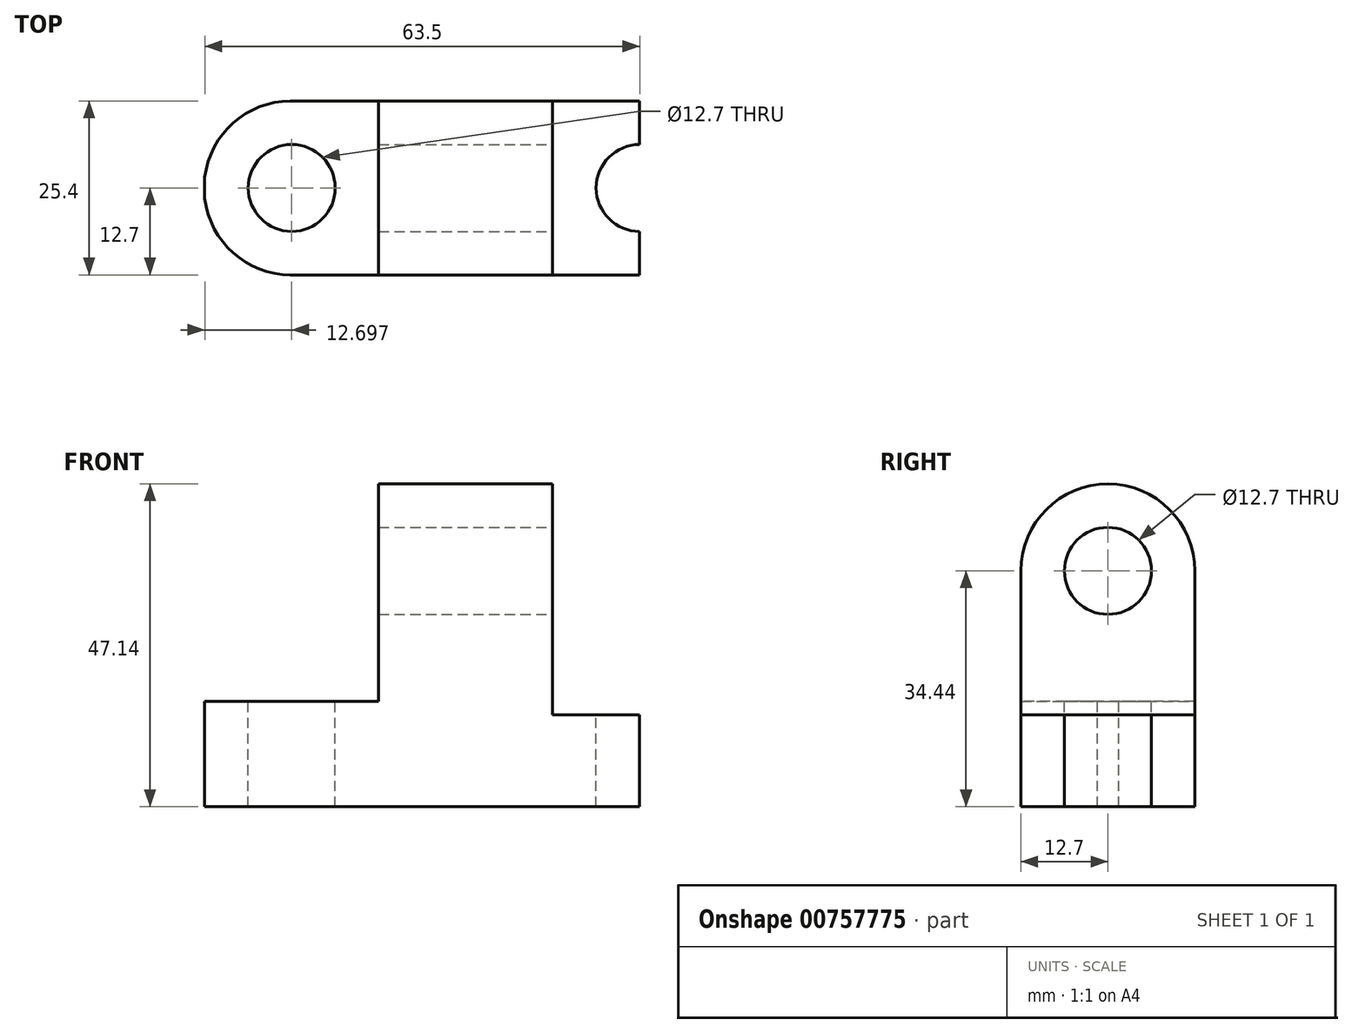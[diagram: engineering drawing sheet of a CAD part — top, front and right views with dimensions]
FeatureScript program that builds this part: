
annotation { "Feature Type Name" : "Feature", "Feature Type Description" : "" }
export const myFeature = defineFeature(function(context is Context, id is Id, definition is map)
    precondition{}
    {
        {
            var Q0;
            Q0=qCreatedBy(makeId("Front.planeOp"),FACE);
            var sketch = newSketch(context, id + "F0", { "sketchPlane" : qUnion([Q0])});
            skLineSegment(sketch, "E0", {"start": v(-30.36, 0) * mm, "end": v(45.84, 0) * mm});
            skLineSegment(sketch, "E1", {"start": v(45.84, 0) * mm, "end": v(45.84, 13.4) * mm});
            skLineSegment(sketch, "E2", {"start": v(45.84, 13.4) * mm, "end": v(20.44, 13.4) * mm});
            skLineSegment(sketch, "E3", {"start": v(20.44, 13.4) * mm, "end": v(20.44, 47.14) * mm});
            skLineSegment(sketch, "E4", {"start": v(20.44, 47.14) * mm, "end": v(-4.96, 47.14) * mm});
            skLineSegment(sketch, "E5", {"start": v(-4.96, 47.14) * mm, "end": v(-4.96, 15.39) * mm});
            skLineSegment(sketch, "E6", {"start": v(-4.96, 15.39) * mm, "end": v(-30.36, 15.39) * mm});
            skLineSegment(sketch, "E7", {"start": v(-30.36, 15.39) * mm, "end": v(-30.36, 0) * mm});
            skSolve(sketch);
        }
        {
            var Q0;
            Q0 = qSketchRegion(id + "F0", true);
            extrude(context, id + "F1", {"entities" : qUnion([Q0]), "depth" : 25.4 * mm, "offsetDistance" : 25.4 * mm});
        }
        {
            var Q0;
            Q0=makeQuery(id+"F1.opExtrude","SWEPT_FACE",FACE,{"disambiguationData":[OSD([sQuery(id+"F0.wireOp",EDGE,"E3")])]});
            var sketch = newSketch(context, id + "F2", { "sketchPlane" : qUnion([Q0])});
            skLineSegment(sketch, "E8", {"start": v(-25.4, 34.44) * mm, "end": v(0, 34.44) * mm});
            skCircle(sketch, "E9", {"center": v(-12.7, 34.44) * mm, "radius": 6.35 * mm});
            skArc(sketch, "E10", {"start": v(0, 34.44) * mm, "mid": v(-12.7, 47.14) * mm, "end": v(-25.4, 34.44) * mm});
            skSolve(sketch);
        }
        {
            var Q0;
            {var subQ0=sQuery(id+"F2.wireOp",EDGE,"E9");var subQ1=sQuery(id+"F2.wireOp",EDGE,"E8");var subQ2=makeQuery(id+"F2.imprint","INTERSECT",VERTEX,{"disambiguationData":[OD(0.0)],"derivedFrom":[subQ1,subQ0]});Q0=makeQuery(id+"F2.imprint","IMPRINT",FACE,{"disambiguationData":[TD([[makeQuery(id+"F2.imprint","IMPRINT",EDGE,{"disambiguationData":[TD([[subQ2,-1.0]])],"derivedFrom":subQ1}),1.0]])]});}
            var Q1;
            {var subQ0=sQuery(id+"F2.wireOp",EDGE,"E10");var subQ1=sQuery(id+"F0.wireOp",EDGE,"E3");var subQ2=makeQuery(id+"F1.opExtrude","CAP_EDGE",EDGE,{"disambiguationData":[OSD([subQ1])],"isStart":false});var subQ3=makeQuery(id+"F2.imprint","INTERSECT",VERTEX,{"derivedFrom":[subQ2,sQuery(id+"F2.wireOp",EDGE,"E8"),subQ0]});Q1=makeQuery(id+"F2.imprint","IMPRINT",FACE,{"disambiguationData":[TD([[makeQuery(id+"F2.imprint","IMPRINT",EDGE,{"disambiguationData":[TD([[subQ3,1.0]])],"derivedFrom":subQ0}),-1.0]])]});}
            var Q2;
            {var subQ0=sQuery(id+"F2.wireOp",EDGE,"E10");var subQ1=sQuery(id+"F0.wireOp",EDGE,"E3");var subQ2=makeQuery(id+"F1.opExtrude","CAP_EDGE",EDGE,{"disambiguationData":[OSD([subQ1])],"isStart":true});var subQ3=makeQuery(id+"F2.imprint","INTERSECT",VERTEX,{"derivedFrom":[subQ2,sQuery(id+"F2.wireOp",EDGE,"E8"),subQ0]});Q2=makeQuery(id+"F2.imprint","IMPRINT",FACE,{"disambiguationData":[TD([[makeQuery(id+"F2.imprint","IMPRINT",EDGE,{"disambiguationData":[TD([[subQ3,-1.0]])],"derivedFrom":subQ0}),-1.0]])]});}
            var Q3;
            {var subQ0=sQuery(id+"F2.wireOp",EDGE,"E9");var subQ1=sQuery(id+"F2.wireOp",EDGE,"E8");var subQ2=makeQuery(id+"F2.imprint","INTERSECT",VERTEX,{"disambiguationData":[OD(0.0)],"derivedFrom":[subQ1,subQ0]});Q3=makeQuery(id+"F2.imprint","IMPRINT",FACE,{"disambiguationData":[TD([[makeQuery(id+"F2.imprint","IMPRINT",EDGE,{"disambiguationData":[TD([[subQ2,-1.0]])],"derivedFrom":subQ1}),-1.0]])]});}
            extrude(context, id + "F3", {"entities" : qUnion([Q0, Q1, Q2, Q3]), "operationType" : NewBodyOperationType.REMOVE, "endBound" : BoundingType.THROUGH_ALL, "oppositeDirection" : true, "depth" : 25.4 * mm, "offsetDistance" : 25.4 * mm});
        }
        {
            var Q0;
            Q0=makeQuery(id+"F1.opExtrude","SWEPT_FACE",FACE,{"disambiguationData":[OSD([sQuery(id+"F0.wireOp",EDGE,"E2")])]});
            var sketch = newSketch(context, id + "F4", { "sketchPlane" : qUnion([Q0])});
            skLineSegment(sketch, "E11", {"start": v(33.14, 0) * mm, "end": v(33.14, -25.4) * mm});
            skCircle(sketch, "E12", {"center": v(33.14, -12.7) * mm, "radius": 6.35 * mm});
            skArc(sketch, "E13", {"start": v(33.14, -25.4) * mm, "mid": v(45.94, -12.7) * mm, "end": v(33.14, 0) * mm});
            skSolve(sketch);
        }
        {
            var Q0;
            {var subQ0=sQuery(id+"F4.wireOp",EDGE,"E12");var subQ1=sQuery(id+"F4.wireOp",EDGE,"E11");var subQ2=makeQuery(id+"F4.imprint","INTERSECT",VERTEX,{"disambiguationData":[OD(0.0)],"derivedFrom":[subQ1,subQ0]});Q0=makeQuery(id+"F4.imprint","IMPRINT",FACE,{"disambiguationData":[TD([[makeQuery(id+"F4.imprint","IMPRINT",EDGE,{"disambiguationData":[TD([[subQ2,-1.0]])],"derivedFrom":subQ1}),-1.0]])]});}
            var Q1;
            {var subQ0=sQuery(id+"F4.wireOp",EDGE,"E12");var subQ1=sQuery(id+"F4.wireOp",EDGE,"E11");var subQ2=makeQuery(id+"F4.imprint","INTERSECT",VERTEX,{"disambiguationData":[OD(0.0)],"derivedFrom":[subQ1,subQ0]});Q1=makeQuery(id+"F4.imprint","IMPRINT",FACE,{"disambiguationData":[TD([[makeQuery(id+"F4.imprint","IMPRINT",EDGE,{"disambiguationData":[TD([[subQ2,-1.0]])],"derivedFrom":subQ1}),1.0]])]});}
            var Q2;
            {var subQ0=sQuery(id+"F4.wireOp",EDGE,"E13");var subQ1=makeQuery(id+"F1.opExtrude","CAP_EDGE",EDGE,{"disambiguationData":[OSD([sQuery(id+"F0.wireOp",EDGE,"E2")])],"isStart":false});var subQ3=makeQuery(id+"F4.imprint","INTERSECT",VERTEX,{"derivedFrom":[subQ1,subQ0]});Q2=makeQuery(id+"F4.imprint","IMPRINT",FACE,{"disambiguationData":[TD([[makeQuery(id+"F4.imprint","IMPRINT",EDGE,{"disambiguationData":[TD([[subQ3,1.0]])],"derivedFrom":subQ0}),1.0]])]});}
            var Q3;
            {var subQ0=sQuery(id+"F4.wireOp",EDGE,"E13");var subQ1=makeQuery(id+"F1.opExtrude","SWEPT_EDGE",EDGE,{"disambiguationData":[OSD([sQuery(id+"F0.wireOp",EDGE,"E1"),sQuery(id+"F0.wireOp",EDGE,"E2")])]});var subQ2=makeQuery(id+"F4.imprint","INTERSECT",VERTEX,{"disambiguationData":[OD(0.0)],"derivedFrom":[subQ1,subQ0]});Q3=makeQuery(id+"F4.imprint","IMPRINT",FACE,{"disambiguationData":[TD([[makeQuery(id+"F4.imprint","IMPRINT",EDGE,{"disambiguationData":[TD([[subQ2,-1.0]])],"derivedFrom":subQ0}),1.0]])]});}
            var Q4;
            {var subQ0=sQuery(id+"F4.wireOp",EDGE,"E13");var subQ1=makeQuery(id+"F1.opExtrude","CAP_EDGE",EDGE,{"disambiguationData":[OSD([sQuery(id+"F0.wireOp",EDGE,"E2")])],"isStart":true});var subQ3=makeQuery(id+"F4.imprint","INTERSECT",VERTEX,{"derivedFrom":[subQ1,subQ0]});Q4=makeQuery(id+"F4.imprint","IMPRINT",FACE,{"disambiguationData":[TD([[makeQuery(id+"F4.imprint","IMPRINT",EDGE,{"disambiguationData":[TD([[subQ3,-1.0]])],"derivedFrom":subQ0}),1.0]])]});}
            var Q5;
            {var subQ0=sQuery(id+"F4.wireOp",EDGE,"E13");var subQ1=sQuery(id+"F0.wireOp",EDGE,"E2");var subQ4=makeQuery(id+"F1.opExtrude","CAP_EDGE",EDGE,{"disambiguationData":[OSD([subQ1])],"isStart":true});var subQ5=makeQuery(id+"F4.imprint","INTERSECT",VERTEX,{"derivedFrom":[subQ4,subQ0]});Q5=makeQuery(id+"F4.imprint","IMPRINT",FACE,{"disambiguationData":[TD([[makeQuery(id+"F4.imprint","IMPRINT",EDGE,{"disambiguationData":[TD([[subQ5,1.0]])],"derivedFrom":subQ0}),-1.0]])]});}
            var Q6;
            {var subQ0=sQuery(id+"F4.wireOp",EDGE,"E13");var subQ1=sQuery(id+"F0.wireOp",EDGE,"E2");var subQ2=makeQuery(id+"F1.opExtrude","CAP_EDGE",EDGE,{"disambiguationData":[OSD([subQ1])],"isStart":false});var subQ3=makeQuery(id+"F4.imprint","INTERSECT",VERTEX,{"derivedFrom":[subQ2,subQ0]});Q6=makeQuery(id+"F4.imprint","IMPRINT",FACE,{"disambiguationData":[TD([[makeQuery(id+"F4.imprint","IMPRINT",EDGE,{"disambiguationData":[TD([[subQ3,-1.0]])],"derivedFrom":subQ0}),-1.0]])]});}
            extrude(context, id + "F5", {"entities" : qUnion([Q0, Q1, Q2, Q3, Q4, Q5, Q6]), "operationType" : NewBodyOperationType.REMOVE, "endBound" : BoundingType.THROUGH_ALL, "oppositeDirection" : true, "depth" : 25.4 * mm, "offsetDistance" : 25.4 * mm});
        }
        {
            var Q0;
            Q0=makeQuery(id+"F1.opExtrude","SWEPT_FACE",FACE,{"disambiguationData":[OSD([sQuery(id+"F0.wireOp",EDGE,"E6")])]});
            var sketch = newSketch(context, id + "F6", { "sketchPlane" : qUnion([Q0])});
            skLineSegment(sketch, "E14", {"start": v(-17.66, 0) * mm, "end": v(-17.66, -25.4) * mm});
            skCircle(sketch, "E15", {"center": v(-17.66, -12.7) * mm, "radius": 6.35 * mm});
            skArc(sketch, "E16", {"start": v(-17.66, 0) * mm, "mid": v(-30.46, -12.7) * mm, "end": v(-17.66, -25.4) * mm});
            skSolve(sketch);
        }
        {
            var Q0;
            {var subQ0=sQuery(id+"F6.wireOp",EDGE,"E15");var subQ1=sQuery(id+"F6.wireOp",EDGE,"E14");var subQ2=makeQuery(id+"F6.imprint","INTERSECT",VERTEX,{"disambiguationData":[OD(0.0)],"derivedFrom":[subQ1,subQ0]});Q0=makeQuery(id+"F6.imprint","IMPRINT",FACE,{"disambiguationData":[TD([[makeQuery(id+"F6.imprint","IMPRINT",EDGE,{"disambiguationData":[TD([[subQ2,-1.0]])],"derivedFrom":subQ1}),-1.0]])]});}
            var Q1;
            {var subQ0=sQuery(id+"F6.wireOp",EDGE,"E15");var subQ1=sQuery(id+"F6.wireOp",EDGE,"E14");var subQ2=makeQuery(id+"F6.imprint","INTERSECT",VERTEX,{"disambiguationData":[OD(0.0)],"derivedFrom":[subQ1,subQ0]});Q1=makeQuery(id+"F6.imprint","IMPRINT",FACE,{"disambiguationData":[TD([[makeQuery(id+"F6.imprint","IMPRINT",EDGE,{"disambiguationData":[TD([[subQ2,-1.0]])],"derivedFrom":subQ1}),1.0]])]});}
            var Q2;
            {var subQ0=sQuery(id+"F6.wireOp",EDGE,"E16");var subQ1=makeQuery(id+"F1.opExtrude","CAP_EDGE",EDGE,{"disambiguationData":[OSD([sQuery(id+"F0.wireOp",EDGE,"E6")])],"isStart":true});var subQ3=makeQuery(id+"F6.imprint","INTERSECT",VERTEX,{"derivedFrom":[subQ1,subQ0]});Q2=makeQuery(id+"F6.imprint","IMPRINT",FACE,{"disambiguationData":[TD([[makeQuery(id+"F6.imprint","IMPRINT",EDGE,{"disambiguationData":[TD([[subQ3,1.0]])],"derivedFrom":subQ0}),1.0]])]});}
            var Q3;
            {var subQ0=sQuery(id+"F6.wireOp",EDGE,"E16");var subQ1=makeQuery(id+"F1.opExtrude","SWEPT_EDGE",EDGE,{"disambiguationData":[OSD([sQuery(id+"F0.wireOp",EDGE,"E6"),sQuery(id+"F0.wireOp",EDGE,"E7")])]});var subQ2=makeQuery(id+"F6.imprint","INTERSECT",VERTEX,{"disambiguationData":[OD(0.0)],"derivedFrom":[subQ1,subQ0]});Q3=makeQuery(id+"F6.imprint","IMPRINT",FACE,{"disambiguationData":[TD([[makeQuery(id+"F6.imprint","IMPRINT",EDGE,{"disambiguationData":[TD([[subQ2,-1.0]])],"derivedFrom":subQ0}),1.0]])]});}
            var Q4;
            {var subQ0=sQuery(id+"F6.wireOp",EDGE,"E16");var subQ1=makeQuery(id+"F1.opExtrude","CAP_EDGE",EDGE,{"disambiguationData":[OSD([sQuery(id+"F0.wireOp",EDGE,"E6")])],"isStart":false});var subQ3=makeQuery(id+"F6.imprint","INTERSECT",VERTEX,{"derivedFrom":[subQ1,subQ0]});Q4=makeQuery(id+"F6.imprint","IMPRINT",FACE,{"disambiguationData":[TD([[makeQuery(id+"F6.imprint","IMPRINT",EDGE,{"disambiguationData":[TD([[subQ3,-1.0]])],"derivedFrom":subQ0}),1.0]])]});}
            var Q5;
            {var subQ0=sQuery(id+"F6.wireOp",EDGE,"E16");var subQ1=sQuery(id+"F0.wireOp",EDGE,"E6");var subQ2=makeQuery(id+"F1.opExtrude","CAP_EDGE",EDGE,{"disambiguationData":[OSD([subQ1])],"isStart":true});var subQ3=makeQuery(id+"F6.imprint","INTERSECT",VERTEX,{"derivedFrom":[subQ2,subQ0]});Q5=makeQuery(id+"F6.imprint","IMPRINT",FACE,{"disambiguationData":[TD([[makeQuery(id+"F6.imprint","IMPRINT",EDGE,{"disambiguationData":[TD([[subQ3,-1.0]])],"derivedFrom":subQ0}),-1.0]])]});}
            var Q6;
            {var subQ0=sQuery(id+"F6.wireOp",EDGE,"E16");var subQ1=sQuery(id+"F0.wireOp",EDGE,"E6");var subQ4=makeQuery(id+"F1.opExtrude","CAP_EDGE",EDGE,{"disambiguationData":[OSD([subQ1])],"isStart":false});var subQ5=makeQuery(id+"F6.imprint","INTERSECT",VERTEX,{"derivedFrom":[subQ4,subQ0]});Q6=makeQuery(id+"F6.imprint","IMPRINT",FACE,{"disambiguationData":[TD([[makeQuery(id+"F6.imprint","IMPRINT",EDGE,{"disambiguationData":[TD([[subQ5,1.0]])],"derivedFrom":subQ0}),-1.0]])]});}
            extrude(context, id + "F7", {"entities" : qUnion([Q0, Q1, Q2, Q3, Q4, Q5, Q6]), "operationType" : NewBodyOperationType.REMOVE, "endBound" : BoundingType.THROUGH_ALL, "oppositeDirection" : true, "depth" : 25.4 * mm, "offsetDistance" : 25.4 * mm});
        }
    });
